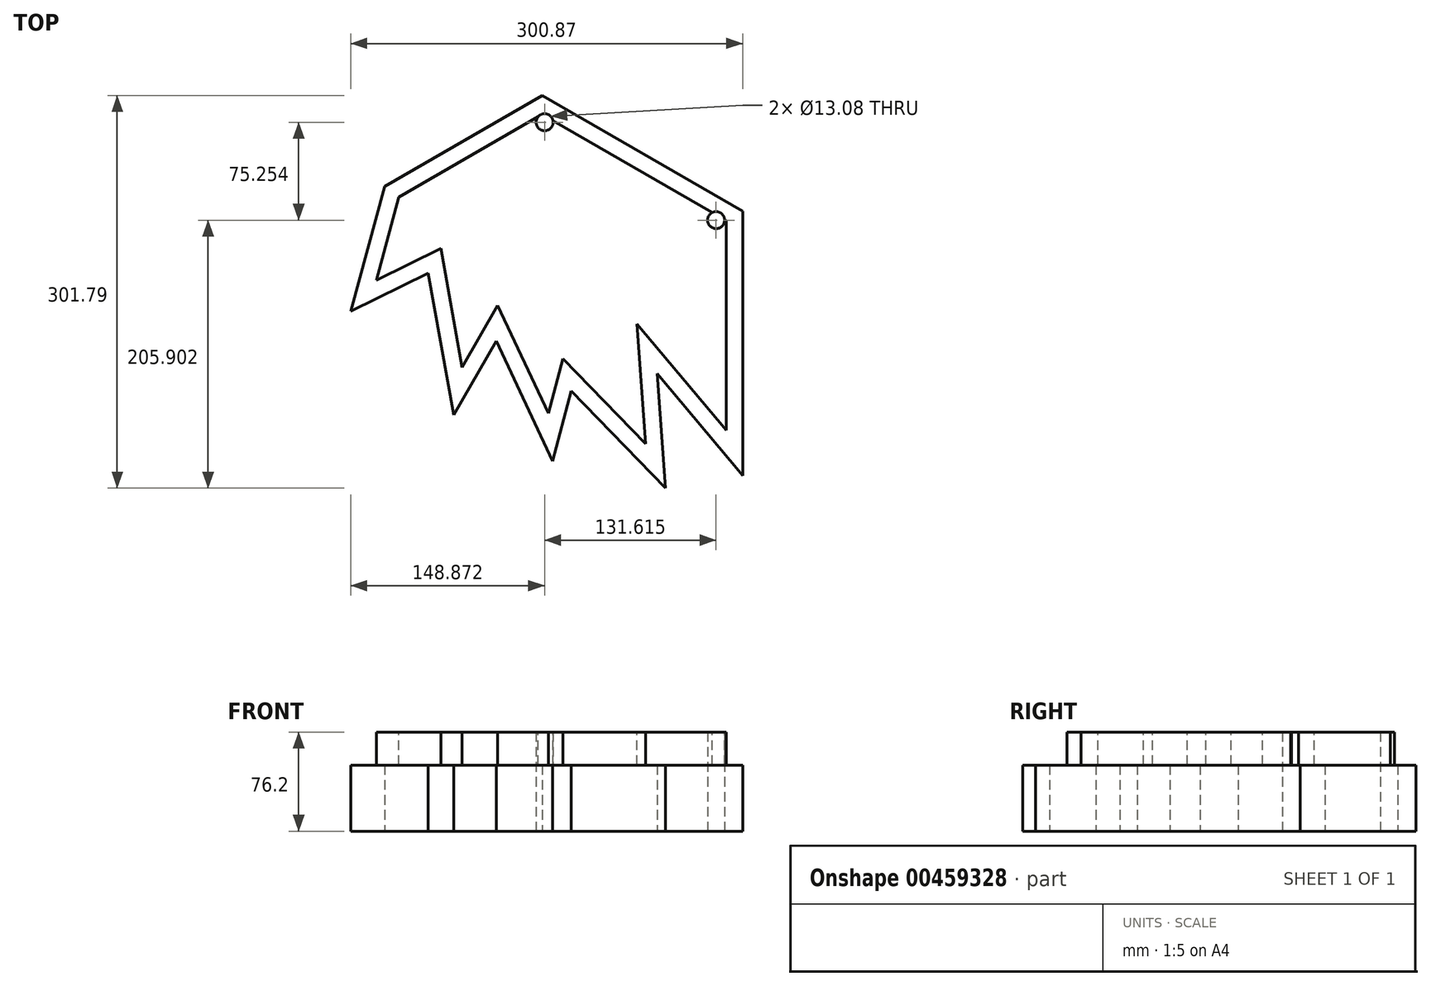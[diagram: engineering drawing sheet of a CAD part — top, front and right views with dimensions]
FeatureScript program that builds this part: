
annotation { "Feature Type Name" : "Feature", "Feature Type Description" : "" }
export const myFeature = defineFeature(function(context is Context, id is Id, definition is map)
    precondition{}
    {
        {
            var Q0;
            Q0=qCreatedBy(makeId("Top.planeOp"),FACE);
            var sketch = newSketch(context, id + "F0", { "sketchPlane" : qUnion([Q0])});
            skLineSegment(sketch, "E0", {"start": v(0, 0) * mm, "end": v(0, 203.2) * mm});
            skLineSegment(sketch, "E1", {"start": v(0, 203.2) * mm, "end": v(-153.98, 292.1) * mm});
            skLineSegment(sketch, "E2", {"start": v(-153.98, 292.1) * mm, "end": v(-274.96, 222.25) * mm});
            skLineSegment(sketch, "E3", {"start": v(-274.96, 222.25) * mm, "end": v(-280.38, 178.13) * mm});
            skLineSegment(sketch, "E4", {"start": v(-280.38, 178.13) * mm, "end": v(-298.27, 127.62) * mm});
            skLineSegment(sketch, "E5", {"start": v(-275.74, 215.95) * mm, "end": v(0, 76.2) * mm});
            skPoint(sketch, "E6", {"position": v(-232.4, 193.99) * mm});
            skPoint(sketch, "E7", {"position": v(-198.24, 176.67) * mm});
            skPoint(sketch, "E8", {"position": v(-158.6, 156.58) * mm});
            skPoint(sketch, "E9", {"position": v(-113.28, 133.61) * mm});
            skPoint(sketch, "E10", {"position": v(-67.97, 110.65) * mm});
            skLineSegment(sketch, "E11", {"start": v(-67.97, 110.65) * mm, "end": v(-59.3, -9.7) * mm});
            skLineSegment(sketch, "E12", {"start": v(-113.28, 133.61) * mm, "end": v(-145.89, 10.87) * mm});
            skLineSegment(sketch, "E13", {"start": v(-158.6, 156.58) * mm, "end": v(-221.86, 46.46) * mm});
            skLineSegment(sketch, "E14", {"start": v(-198.24, 176.67) * mm, "end": v(-300.87, 126.35) * mm});
            skLineSegment(sketch, "E15", {"start": v(-59.3, -9.7) * mm, "end": v(-131.56, 64.82) * mm});
            skLineSegment(sketch, "E16", {"start": v(-145.89, 10.87) * mm, "end": v(-189.22, 103.27) * mm});
            skLineSegment(sketch, "E17", {"start": v(-221.86, 46.46) * mm, "end": v(-241.33, 155.54) * mm});
            skLineSegment(sketch, "E18", {"start": v(0, 0) * mm, "end": v(-65.63, 78.22) * mm});
            skCircle(sketch, "E19", {"center": v(-20.38, 196.21) * mm, "radius": 6.54 * mm});
            skCircle(sketch, "E20", {"center": v(-152, 271.47) * mm, "radius": 6.54 * mm});
            skLineSegment(sketch, "E21", {"start": v(-274.96, 222.25) * mm, "end": v(-300.87, 126.35) * mm});
            skSolve(sketch);
        }
        {
            var Q0;
            {var subQ9=sQuery(id+"F0.wireOp",EDGE,"E1");Q0=makeQuery(id+"F0.imprint","IMPRINT",FACE,{"disambiguationData":[TD([[makeQuery(id+"F0.imprint","IMPRINT",EDGE,{"derivedFrom":subQ9}),1.0]])]});}
            var Q1;
            {var subQ6=sQuery(id+"F0.wireOp",EDGE,"E4");Q1=makeQuery(id+"F0.imprint","IMPRINT",FACE,{"disambiguationData":[TD([[makeQuery(id+"F0.imprint","IMPRINT",EDGE,{"derivedFrom":subQ6}),1.0]])]});}
            var Q2;
            {var subQ0=sQuery(id+"F0.wireOp",EDGE,"E4");Q2=makeQuery(id+"F0.imprint","IMPRINT",FACE,{"disambiguationData":[TD([[makeQuery(id+"F0.imprint","IMPRINT",EDGE,{"derivedFrom":subQ0}),-1.0]])]});}
            var Q3;
            {var subQ0=sQuery(id+"F0.wireOp",EDGE,"E17");Q3=makeQuery(id+"F0.imprint","IMPRINT",FACE,{"disambiguationData":[TD([[makeQuery(id+"F0.imprint","IMPRINT",EDGE,{"derivedFrom":subQ0}),-1.0]])]});}
            var Q4;
            {var subQ3=sQuery(id+"F0.wireOp",EDGE,"E16");Q4=makeQuery(id+"F0.imprint","IMPRINT",FACE,{"disambiguationData":[TD([[makeQuery(id+"F0.imprint","IMPRINT",EDGE,{"derivedFrom":subQ3}),-1.0]])]});}
            var Q5;
            {var subQ3=sQuery(id+"F0.wireOp",EDGE,"E15");Q5=makeQuery(id+"F0.imprint","IMPRINT",FACE,{"disambiguationData":[TD([[makeQuery(id+"F0.imprint","IMPRINT",EDGE,{"derivedFrom":subQ3}),-1.0]])]});}
            var Q6;
            {var subQ0=sQuery(id+"F0.wireOp",EDGE,"E18");Q6=makeQuery(id+"F0.imprint","IMPRINT",FACE,{"disambiguationData":[TD([[makeQuery(id+"F0.imprint","IMPRINT",EDGE,{"derivedFrom":subQ0}),-1.0]])]});}
            extrude(context, id + "F1", {"entities" : qUnion([Q0, Q1, Q2, Q3, Q4, Q5, Q6]), "depth" : 76.2 * mm});
        }
        {
            var Q0;
            Q0=makeQuery(id+"F1.opExtrude","CAP_FACE",FACE,{"disambiguationData":[OSD([sQuery(id+"F0.wireOp",EDGE,"E0"),sQuery(id+"F0.wireOp",EDGE,"E1"),sQuery(id+"F0.wireOp",EDGE,"E2"),sQuery(id+"F0.wireOp",EDGE,"E11"),sQuery(id+"F0.wireOp",EDGE,"E12"),sQuery(id+"F0.wireOp",EDGE,"E13"),sQuery(id+"F0.wireOp",EDGE,"E14"),sQuery(id+"F0.wireOp",EDGE,"E15"),sQuery(id+"F0.wireOp",EDGE,"E16"),sQuery(id+"F0.wireOp",EDGE,"E17"),sQuery(id+"F0.wireOp",EDGE,"E18"),sQuery(id+"F0.wireOp",EDGE,"E19"),sQuery(id+"F0.wireOp",EDGE,"E20"),sQuery(id+"F0.wireOp",EDGE,"E21")])],"isStart":false});
            var sketch = newSketch(context, id + "F2", { "sketchPlane" : qUnion([Q0])});
            skLineSegment(sketch, "E22.0", {"start": v(-12.7, 195.87) * mm, "end": v(-153.98, 277.44) * mm});
            skLineSegment(sketch, "E22.1", {"start": v(-188.08, 130.75) * mm, "end": v(-215.49, 83.04) * mm});
            skLineSegment(sketch, "E22.2", {"start": v(-215.49, 83.04) * mm, "end": v(-231.8, 174.36) * mm});
            skLineSegment(sketch, "E22.3", {"start": v(-231.8, 174.36) * mm, "end": v(-281.3, 150.09) * mm});
            skLineSegment(sketch, "E22.4", {"start": v(-264.07, 213.87) * mm, "end": v(-281.3, 150.09) * mm});
            skLineSegment(sketch, "E22.5", {"start": v(-149.2, 47.85) * mm, "end": v(-188.08, 130.75) * mm});
            skLineSegment(sketch, "E22.6", {"start": v(-153.98, 277.44) * mm, "end": v(-264.07, 213.87) * mm});
            skLineSegment(sketch, "E22.7", {"start": v(-138.07, 89.77) * mm, "end": v(-149.2, 47.85) * mm});
            skLineSegment(sketch, "E22.8", {"start": v(-74.47, 24.2) * mm, "end": v(-138.07, 89.77) * mm});
            skLineSegment(sketch, "E22.9", {"start": v(-81.12, 116.43) * mm, "end": v(-74.47, 24.2) * mm});
            skLineSegment(sketch, "E22.10", {"start": v(-12.7, 34.9) * mm, "end": v(-81.12, 116.43) * mm});
            skLineSegment(sketch, "E22.11", {"start": v(-12.7, 34.9) * mm, "end": v(-12.7, 195.87) * mm});
            skSolve(sketch);
        }
        {
            var Q0;
            Q0=makeQuery(id+"F2.imprint","IMPRINT",FACE,{"disambiguationData":[TD([[makeQuery(id+"F2.imprint","IMPRINT",EDGE,{"derivedFrom":sQuery(id+"F2.wireOp",EDGE,"E22.1")}),1.0]])]});
            extrude(context, id + "F3", {"entities" : qUnion([Q0]), "operationType" : NewBodyOperationType.REMOVE, "oppositeDirection" : true, "depth" : 25.4 * mm});
        }
    });
